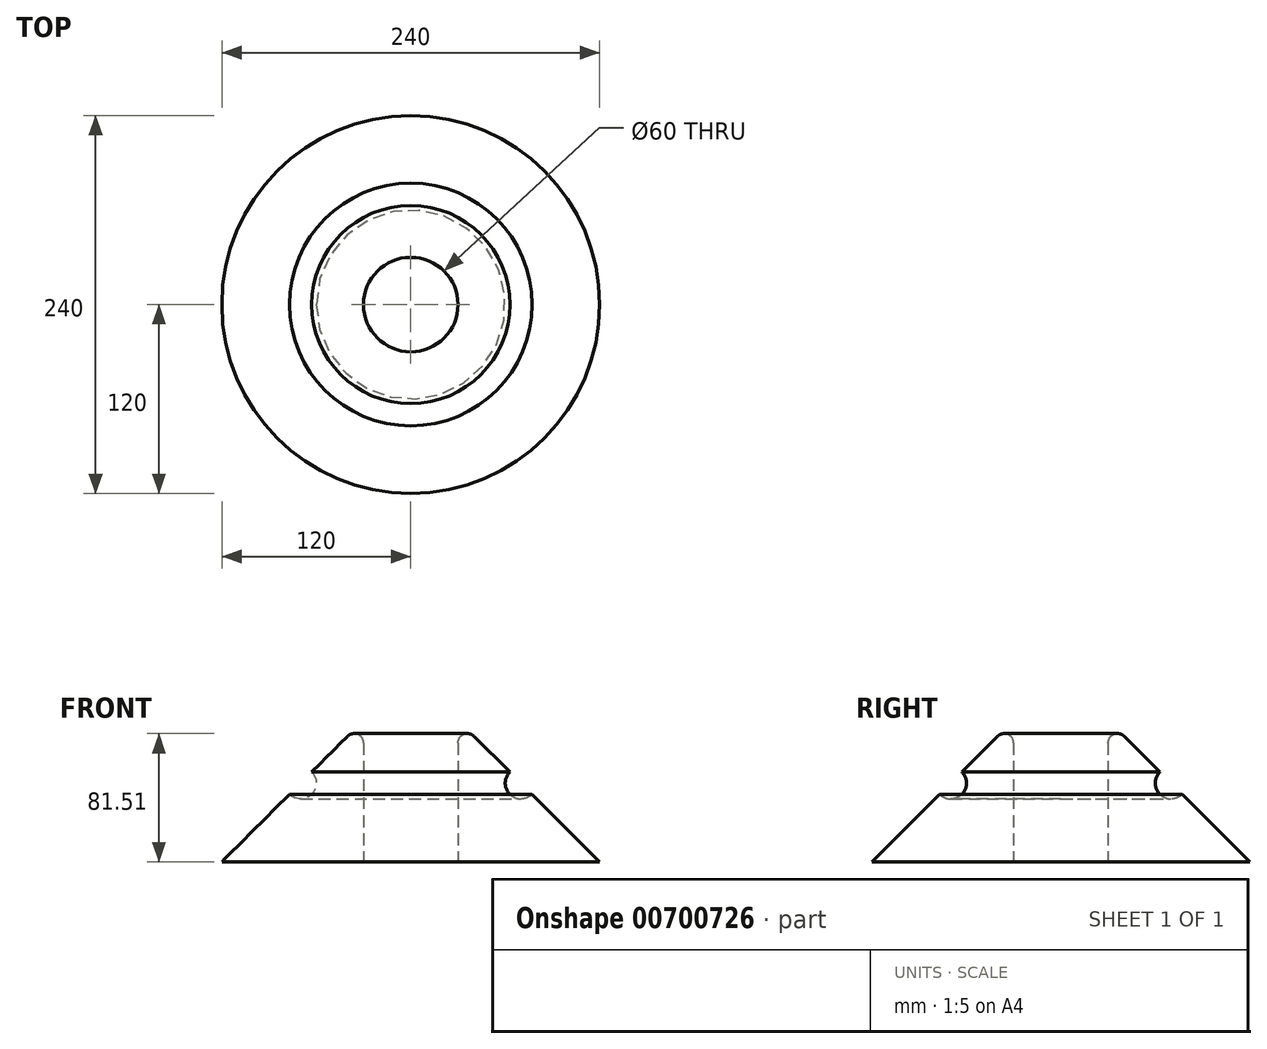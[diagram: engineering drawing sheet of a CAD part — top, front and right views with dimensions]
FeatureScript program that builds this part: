
annotation { "Feature Type Name" : "Feature", "Feature Type Description" : "" }
export const myFeature = defineFeature(function(context is Context, id is Id, definition is map)
    precondition{}
    {
        {
            var Q0;
            Q0=qCreatedBy(makeId("Right.planeOp"),FACE);
            var sketch = newSketch(context, id + "F0", { "sketchPlane" : qUnion([Q0])});
            skLineSegment(sketch, "E0", {"start": v(-30, 0) * mm, "end": v(-30, 75.51) * mm});
            skLineSegment(sketch, "E1", {"start": v(-40.24, 79.76) * mm, "end": v(-120, 0) * mm});
            skLineSegment(sketch, "E2", {"start": v(-120, 0) * mm, "end": v(-30, 0) * mm});
            skPoint(sketch, "E3.visualSharp", {"position": v(-30, 90) * mm});
            skArc(sketch, "E3.filletArc", {"start": v(-30, 75.51) * mm, "mid": v(-33.7, 81.06) * mm, "end": v(-40.24, 79.76) * mm});
            skSolve(sketch);
        }
        {
            var Q0;
            Q0=qCreatedBy(makeId("Right.planeOp"),FACE);
            var sketch = newSketch(context, id + "F1", { "sketchPlane" : qUnion([Q0])});
            skLineSegment(sketch, "E4", {"start": v(0, 0) * mm, "end": v(0, 103.75) * mm, "construction": true});
            skSolve(sketch);
        }
        {
            var Q0;
            Q0=makeQuery(id+"F0.imprint","IMPRINT",FACE,{"disambiguationData":[TD([[makeQuery(id+"F0.imprint","IMPRINT",EDGE,{"derivedFrom":sQuery(id+"F0.wireOp",EDGE,"E0")}),1.0]])]});
            var Q1;
            Q1=sQuery(id+"F1.wireOp",EDGE,"E4");
            revolve(context, id + "F2", {"entities" : qUnion([Q0]), "axis" : qUnion([Q1]), "revolveType" : RevolveType.FULL});
        }
        {
            var Q0;
            Q0=qCreatedBy(makeId("Front.planeOp"),FACE);
            var sketch = newSketch(context, id + "F3", { "sketchPlane" : qUnion([Q0])});
            skCircle(sketch, "E5", {"center": v(70, 50) * mm, "radius": 10 * mm});
            skSolve(sketch);
        }
        {
            var Q0;
            Q0=qCreatedBy(makeId("Front.planeOp"),FACE);
            var sketch = newSketch(context, id + "F4", { "sketchPlane" : qUnion([Q0])});
            skLineSegment(sketch, "E6", {"start": v(0, 0) * mm, "end": v(0, 99.75) * mm});
            skSolve(sketch);
        }
        {
            var Q0;
            Q0=makeQuery(id+"F3.imprint","IMPRINT",FACE,{"disambiguationData":[TD([[makeQuery(id+"F3.imprint","IMPRINT",EDGE,{"derivedFrom":sQuery(id+"F3.wireOp",EDGE,"E5")}),1.0]])]});
            var Q1;
            Q1=sQuery(id+"F4.wireOp",EDGE,"E6");
            revolve(context, id + "F5", {"operationType" : NewBodyOperationType.REMOVE, "entities" : qUnion([Q0]), "axis" : qUnion([Q1]), "revolveType" : RevolveType.FULL, "oppositeDirection" : true});
        }
    });
